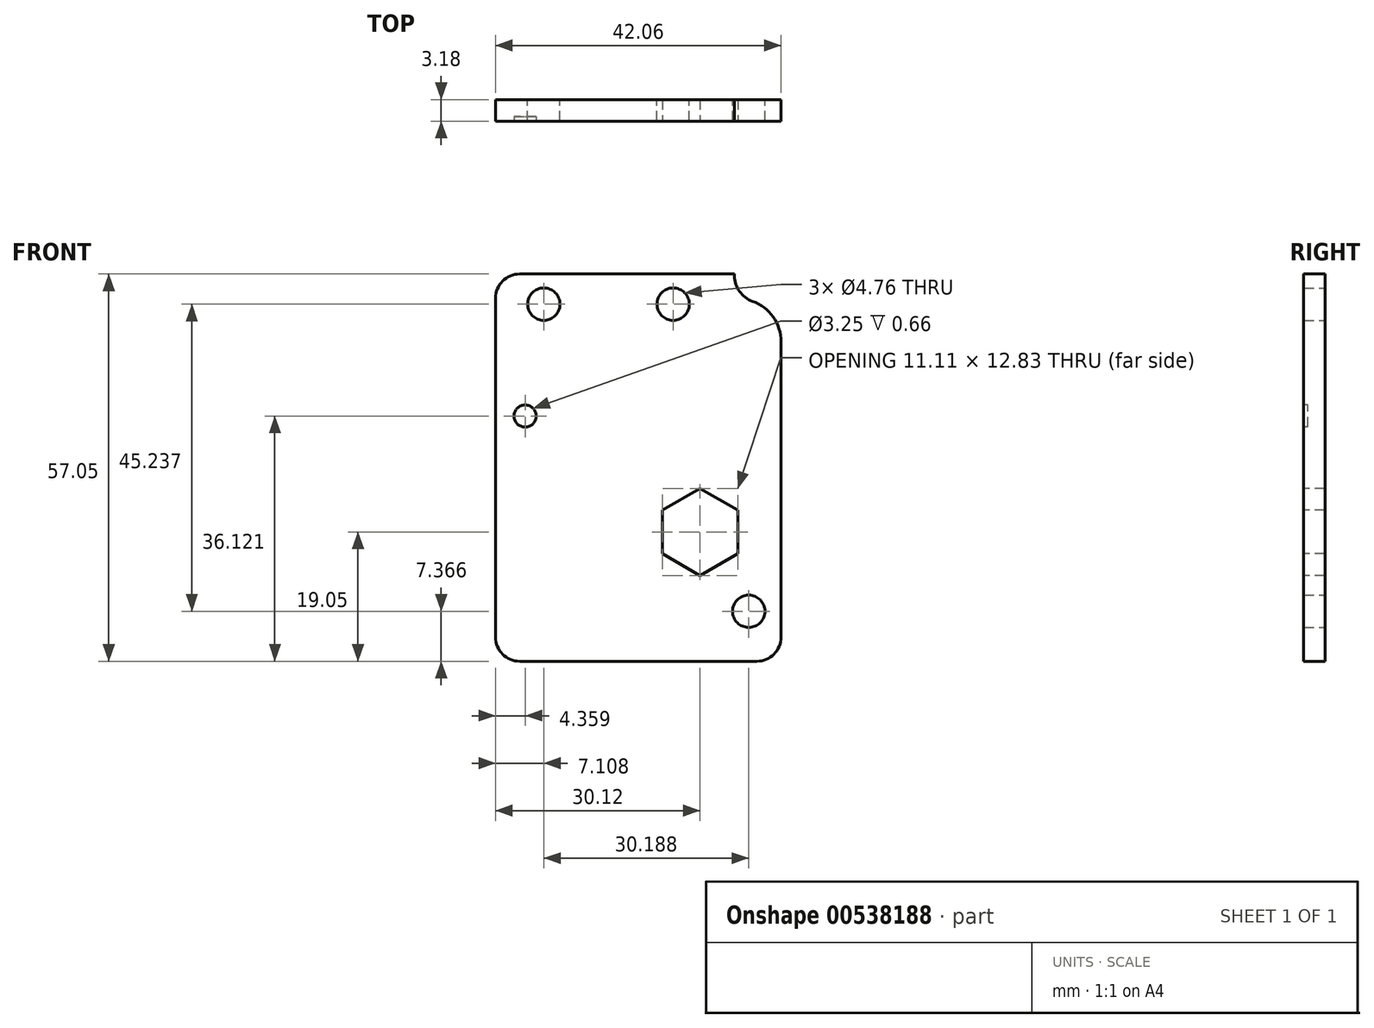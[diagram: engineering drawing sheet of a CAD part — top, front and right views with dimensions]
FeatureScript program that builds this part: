
annotation { "Feature Type Name" : "Feature", "Feature Type Description" : "" }
export const myFeature = defineFeature(function(context is Context, id is Id, definition is map)
    precondition{}
    {
        {
            var Q0;
            Q0=qCreatedBy(makeId("Front.planeOp"),FACE);
            var sketch = newSketch(context, id + "F0", { "sketchPlane" : qUnion([Q0])});
            skLineSegment(sketch, "E0", {"start": v(-26.55, -19.05) * mm, "end": v(8.37, -19.05) * mm});
            skLineSegment(sketch, "E1", {"start": v(-30.12, 34.43) * mm, "end": v(-30.12, -15.48) * mm});
            skArc(sketch, "E2", {"start": v(-30.12, -15.48) * mm, "mid": v(-29.08, -18) * mm, "end": v(-26.55, -19.05) * mm});
            skArc(sketch, "E3", {"start": v(8.37, -19.05) * mm, "mid": v(10.9, -18) * mm, "end": v(11.94, -15.48) * mm});
            skArc(sketch, "E4", {"start": v(-26.55, 38) * mm, "mid": v(-29.08, 36.95) * mm, "end": v(-30.12, 34.43) * mm});
            skCircle(sketch, "E5", {"center": v(-23.01, 33.55) * mm, "radius": 2.38 * mm});
            skCircle(sketch, "E6", {"center": v(-3.96, 33.55) * mm, "radius": 2.38 * mm});
            skLineSegment(sketch, "E7", {"start": v(5.08, 38) * mm, "end": v(-26.55, 38) * mm});
            skLineSegment(sketch, "E8", {"start": v(11.94, -15.48) * mm, "end": v(11.94, 28) * mm});
            skLineSegment(sketch, "E9", {"start": v(5.08, 37.72) * mm, "end": v(5.08, 38) * mm});
            skArc(sketch, "E10", {"start": v(5.08, 37.72) * mm, "mid": v(5.8, 35.43) * mm, "end": v(7.72, 33.98) * mm});
            skCircle(sketch, "E11", {"center": v(7.18, -11.68) * mm, "radius": 2.38 * mm});
            skCircle(sketch, "E12", {"center": v(0, 0) * mm, "radius": 3.18 * mm});
            skArc(sketch, "E13.filletArc", {"start": v(11.94, 28) * mm, "mid": v(10.78, 31.66) * mm, "end": v(7.72, 33.98) * mm});
            skLineSegment(sketch, "E14", {"start": v(-23.01, 33.55) * mm, "end": v(-3.96, 33.55) * mm, "construction": true});
            skSolve(sketch);
        }
        {
            var Q0;
            Q0=makeQuery(id+"F0.imprint","IMPRINT",FACE,{"disambiguationData":[TD([[makeQuery(id+"F0.imprint","IMPRINT",EDGE,{"derivedFrom":sQuery(id+"F0.wireOp",EDGE,"E0")}),1.0]])]});
            extrude(context, id + "F1", {"entities" : qUnion([Q0]), "depth" : 3.17 * mm, "offsetDistance" : 25.4 * mm});
        }
        {
            var Q0;
            Q0=makeQuery(id+"F1.opExtrude","CAP_FACE",FACE,{"disambiguationData":[OSD([sQuery(id+"F0.wireOp",EDGE,"E0"),sQuery(id+"F0.wireOp",EDGE,"E1"),sQuery(id+"F0.wireOp",EDGE,"E2"),sQuery(id+"F0.wireOp",EDGE,"E3"),sQuery(id+"F0.wireOp",EDGE,"E4"),sQuery(id+"F0.wireOp",EDGE,"E5"),sQuery(id+"F0.wireOp",EDGE,"E6"),sQuery(id+"F0.wireOp",EDGE,"E7"),sQuery(id+"F0.wireOp",EDGE,"E8"),sQuery(id+"F0.wireOp",EDGE,"E9"),sQuery(id+"F0.wireOp",EDGE,"E10"),sQuery(id+"F0.wireOp",EDGE,"E11"),sQuery(id+"F0.wireOp",EDGE,"E12"),sQuery(id+"F0.wireOp",EDGE,"E13.filletArc")])],"isStart":false});
            var sketch = newSketch(context, id + "F2", { "sketchPlane" : qUnion([Q0])});
            skCircle(sketch, "E15.cCircle", {"center": v(0, 0) * mm, "radius": 5.56 * mm, "construction": true});
            skLineSegment(sketch, "E15.0", {"start": v(-5.56, 3.2) * mm, "end": v(0, 6.42) * mm});
            skLineSegment(sketch, "E15.1", {"start": v(0, 6.42) * mm, "end": v(5.56, 3.2) * mm});
            skLineSegment(sketch, "E15.2", {"start": v(5.56, 3.2) * mm, "end": v(5.56, -3.2) * mm});
            skLineSegment(sketch, "E15.3", {"start": v(5.56, -3.2) * mm, "end": v(0, -6.42) * mm});
            skLineSegment(sketch, "E15.4", {"start": v(0, -6.42) * mm, "end": v(-5.56, -3.2) * mm});
            skLineSegment(sketch, "E15.5", {"start": v(-5.56, -3.2) * mm, "end": v(-5.56, 3.2) * mm});
            skPoint(sketch, "E15.0.midPoint", {"position": v(-2.78, 4.81) * mm});
            skSolve(sketch);
        }
        {
            var Q0;
            Q0 = qSketchRegion(id + "F2", true);
            extrude(context, id + "F3", {"entities" : qUnion([Q0]), "operationType" : NewBodyOperationType.REMOVE, "endBound" : BoundingType.THROUGH_ALL, "oppositeDirection" : true, "depth" : 25.4 * mm, "offsetDistance" : 25.4 * mm});
        }
        {
            var Q0;
            Q0=makeQuery(id+"F1.opExtrude","CAP_FACE",FACE,{"disambiguationData":[OSD([sQuery(id+"F0.wireOp",EDGE,"E0"),sQuery(id+"F0.wireOp",EDGE,"E1"),sQuery(id+"F0.wireOp",EDGE,"E2"),sQuery(id+"F0.wireOp",EDGE,"E3"),sQuery(id+"F0.wireOp",EDGE,"E4"),sQuery(id+"F0.wireOp",EDGE,"E5"),sQuery(id+"F0.wireOp",EDGE,"E6"),sQuery(id+"F0.wireOp",EDGE,"E7"),sQuery(id+"F0.wireOp",EDGE,"E8"),sQuery(id+"F0.wireOp",EDGE,"E9"),sQuery(id+"F0.wireOp",EDGE,"E10"),sQuery(id+"F0.wireOp",EDGE,"E11"),sQuery(id+"F0.wireOp",EDGE,"E12"),sQuery(id+"F0.wireOp",EDGE,"E13.filletArc")])],"isStart":false});
            var sketch = newSketch(context, id + "F4", { "sketchPlane" : qUnion([Q0])});
            skCircle(sketch, "E16", {"center": v(-25.76, 17.07) * mm, "radius": 1.63 * mm});
            skSolve(sketch);
        }
        {
            var Q0;
            Q0=makeQuery(id+"F4.imprint","IMPRINT",FACE,{"disambiguationData":[TD([[makeQuery(id+"F4.imprint","IMPRINT",EDGE,{"derivedFrom":sQuery(id+"F4.wireOp",EDGE,"E16")}),1.0]])]});
            extrude(context, id + "F5", {"entities" : qUnion([Q0]), "operationType" : NewBodyOperationType.REMOVE, "oppositeDirection" : true, "depth" : 0.66 * mm, "offsetDistance" : 25.4 * mm});
        }
    });
